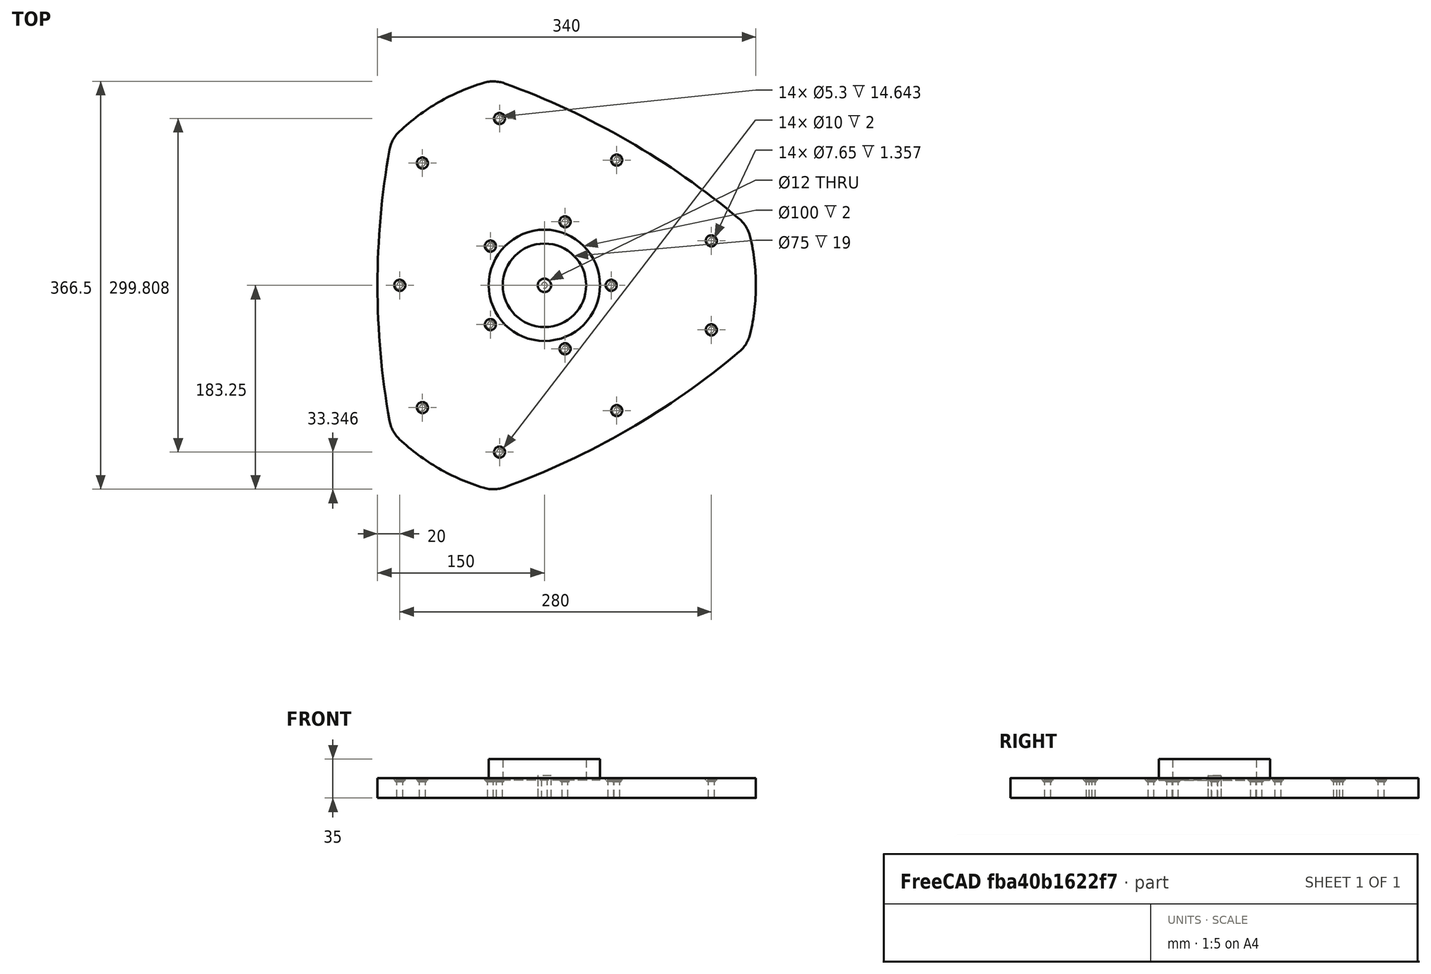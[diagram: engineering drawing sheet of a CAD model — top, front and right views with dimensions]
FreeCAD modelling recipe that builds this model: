
FCSTD DOCUMENT  (FreeCAD 1.1R38827 (Git))
Label: composit_stand3_basement_amplifier_model
License: All rights reserved
LicenseURL: http://en.wikipedia.org/wiki/All_rights_reserved
objects: Part::FeaturePython×6, App::Link×5, PartDesign::CoordinateSystem×3, PartDesign::SubShapeBinder×2, Part::Mirroring×1, Part::Compound×1, PartDesign::Pad×1, Part::Cylinder×1, Part::MultiFuse×1, PartDesign::Boolean×1, PartDesign::Body×1
note: 21 computed .brp shape members not serialized (recipe doc carries the construction recipe); baked Part::Feature solids carry a one-line shape summary decoded from their .brp
EXTERNAL_REF file=composit_stand3_basement_amplifier_main.FCStd obj=Sketch
EXTERNAL_REF file=composit_stand3_basement_amplifier_main.FCStd obj=Join001
EXTERNAL_REF file=composit_stand3_basement_amplifier_main.FCStd obj=Cylinder
EXTERNAL_REF file=composit_stand3_basement_bearing_holder_main.FCStd obj=Placment
EXTERNAL_REF file=../bearing_d100.FCStd obj=Body
EXTERNAL_REF file=composit_stand3_basement_amplifier_main.FCStd obj=Body

FEATURE [PartDesign::SubShapeBinder] Binder
  BindCopyOnChange = 0
  BindMode = 0
  ClaimChildren = false
  Fuse = false
  MakeFace = true
  OffsetFill = false
  OffsetIntersection = false
  OffsetJoinType = 0
  OffsetOpenResult = false
  PartialLoad = false
  Relative = true
  Support = -> [<external composit_stand3_basement_amplifier_main.FCStd>#Sketch]
  _Version = 2
FEATURE [Part::Mirroring] Part__Mirroring  label="Binder (Mirror #1)"
  Base = (0,0,0)
  Normal = (0,1,0)
  Source = -> Binder
FEATURE [Part::FeaturePython] PolarArray  # WARN: FeaturePython — macro-defined, semantics opaque (R4)
  Alignment = 0
  AttacherType = Attacher::AttachEngine3D
  CellStart = A1
  Count = 3
  DistributionLaw = 0
  EndInclusive = false
  ExposePlacement = false
  FlipX = false
  FlipZ = false
  GeneratorMode = 0
  MarkerShape = 1
  MarkerSize = 0
  NumElements = 3
  OrientMode = 2
  Radius = 100
  Reverse = false
  SpanEnd = 360
  SpanStart = 0
  Step = 120
  Type = lattice2PolarArray2.PolarArray
  UseArcRadius = false
  UseArcRange = 0
  VSGVersion = 1
  Values = 0.0 | 120.0 | 240.0
  ValuesSource = 2
  isLattice = 1
FEATURE [Part::Compound] Compound
  Links = -> [Binder,Part__Mirroring]
FEATURE [Part::FeaturePython] Populate  label="Populate PolarArray with Compound"  # WARN: FeaturePython — macro-defined, semantics opaque (R4)
  Copying = 0
  ExposePlacement = false
  MarkerShape = 1
  MarkerSize = 0
  NumElements = 0
  Object = -> Compound
  OutputCompounding = 1
  PlacementsTo = -> PolarArray
  Referencing = 1
  Type = lattice2PopulateCopies.LatticePopulateCopies
  isLattice = 0
FEATURE [Part::FeaturePython] Connect  # WARN: FeaturePython — macro-defined, semantics opaque (R4)
  Objects = -> [Populate]
  Tolerance = 0
FEATURE [PartDesign::SubShapeBinder] Binder001
  BindCopyOnChange = 0
  BindMode = 0
  ClaimChildren = true
  Context = -> Body [Binder001.]
  Fuse = false
  MakeFace = false
  OffsetFill = false
  OffsetIntersection = false
  OffsetJoinType = 0
  OffsetOpenResult = false
  PartialLoad = false
  Relative = true
  Support = -> [Connect]
  _Version = 2
FEATURE [PartDesign::Pad] Pad
  Direction = (0,0,1)
  Length = 18
  Length2 = 10
  Profile = -> Binder001
  Refine = true
  Suppressed = false
  Type = 0
FEATURE [App::Link] Link  label="Populate PolarArray with Join"
  LinkedObject = -> <external composit_stand3_basement_amplifier_main.FCStd>#Join001
FEATURE [Part::Cylinder] Cylinder  label="hole_5,2_mm"
  Angle = 360
  AttacherType = Attacher::AttachEngine3D
  FirstAngle = 0
  Height = 18
  Radius = 2.6
  SecondAngle = 0
FEATURE [Part::FeaturePython] Join  label="holes_placements"  # WARN: FeaturePython — macro-defined, semantics opaque (R4)
  ExposePlacement = false
  Interleave = false
  Links = -> [Link]
  MarkerShape = 1
  MarkerSize = 0
  NumElements = 14
  Type = lattice2JoinArrays.JoinArrays
  isLattice = 1
FEATURE [App::Link] Link001  label="axis_bolt"
  LinkedObject = -> <external composit_stand3_basement_amplifier_main.FCStd>#Cylinder
FEATURE [PartDesign::CoordinateSystem] Local_CS  label="bottom_LCS"
  AttacherType = Attacher::AttachEngine3D
  AttachmentSupport = -> [XY_Plane]
  MapMode = 5
FEATURE [PartDesign::CoordinateSystem] Local_CS001  label="top_LCS"
  AttacherType = Attacher::AttachEngine3D
  AttachmentOffset = pos=(0,0,18) rot=(0,0,1;0rad)
  AttachmentSupport = -> [XY_Plane]
  MapMode = 5
  Placement = pos=(0,0,18) rot=(0,0,1;0rad)
FEATURE [App::Link] Link002  label="bearing_placement"
  LinkTransform = true
  LinkedObject = -> <external composit_stand3_basement_bearing_holder_main.FCStd>#Placment
FEATURE [App::Link] Link003  label="Body"
  LinkedObject = -> <external ../bearing_d100.FCStd>#Body
FEATURE [Part::FeaturePython] Populate002  label="Populate bearing_placement with Body"  # WARN: FeaturePython — macro-defined, semantics opaque (R4)
  Copying = 0
  ExposePlacement = false
  MarkerShape = 1
  MarkerSize = 0
  NumElements = 0
  Object = -> Link003
  OutputCompounding = 2
  PlacementsTo = -> Link002
  Referencing = 0
  Type = lattice2PopulateCopies.LatticePopulateCopies
  isLattice = 0
FEATURE [PartDesign::CoordinateSystem] Local_CS002  label="bearing_LCS"
  AttacherType = Attacher::AttachEngine3D
  AttachmentOffset = pos=(0,0,16) rot=(0,0,1;0rad)
  AttachmentSupport = -> [XY_Plane]
  MapMode = 5
  Placement = pos=(0,0,16) rot=(0,0,1;0rad)
  expr: AttachmentOffset = <<bearing_placement>>.LinkedObject.Placement
FEATURE [App::Link] Link004  label="screw"
  LinkedObject = -> <external composit_stand3_basement_amplifier_main.FCStd>#Body
FEATURE [Part::FeaturePython] Populate001  label="Populate Populate PolarArray with Join with hole_5_mm"  # WARN: FeaturePython — macro-defined, semantics opaque (R4)
  Copying = 0
  ExposePlacement = false
  MarkerShape = 1
  MarkerSize = 0
  NumElements = 0
  Object = -> Link004
  OutputCompounding = 1
  PlacementsTo = -> Join
  Referencing = 0
  Type = lattice2PopulateCopies.LatticePopulateCopies
  isLattice = 0
FEATURE [Part::MultiFuse] Fusion
  Shapes = -> [Populate001,Link001,Populate002]
FEATURE [PartDesign::Boolean] Boolean
  BaseFeature = -> Pad
  Group = -> [Fusion]
  Suppressed = false
  Type = 1
  UsePlacement = true
FEATURE [PartDesign::Body] Body  label="amplifier"
  AllowCompound = false
  Group = -> [Binder001,Pad,Boolean,Local_CS,Local_CS001,Local_CS002]
  Origin = -> Origin
  Tip = -> Boolean

RESOLVED EXTERNAL PARTS (link-assembly join: the EXTERNAL_REF files above that resolve inside this repo's crawl, each included once):
---- part ../bearing_d100.FCStd = doc fcstd_fc5883dd0358 ----
FCSTD DOCUMENT  (FreeCAD 1.1R38827 (Git))
Label: bearing_d100
License: All rights reserved
LicenseURL: http://en.wikipedia.org/wiki/All_rights_reserved
objects: PartDesign::CoordinateSystem×2, Sketcher::SketchObject×1, PartDesign::SubShapeBinder×1, PartDesign::Revolution×1, PartDesign::Body×1
note: 9 computed .brp shape members not serialized (recipe doc carries the construction recipe); baked Part::Feature solids carry a one-line shape summary decoded from their .brp

FEATURE [Sketcher::SketchObject] Sketch  label="main_Sketch"
  ArcFitTolerance = 0
  FullyConstrained = true
  MakeInternals = false
  Placement = pos=(0,0,0) rot=(1,0,0;1.5708rad)
  sketch-geometry (4):
    g0: LineSegment StartX=37.5 StartY=0 StartZ=0 EndX=50 EndY=0 EndZ=0
    g1: LineSegment StartX=50 StartY=0 StartZ=0 EndX=50 EndY=19 EndZ=0
    g2: LineSegment StartX=50 StartY=19 StartZ=0 EndX=37.5 EndY=19 EndZ=0
    g3: LineSegment StartX=37.5 StartY=19 StartZ=0 EndX=37.5 EndY=0 EndZ=0
  constraints (12):
    c: Coincident(g0,g1)
    c: Coincident(g1,g2)
    c: Coincident(g2,g3)
    c: Coincident(g3,g0)
    c: Horizontal(g0)
    c: Horizontal(g2)
    c: Vertical(g1)
    c: Vertical(g3)
    c: PointOnObject(g0,g-1)
    c: DistanceX(g0) = 37.5  'min_r'
    c: DistanceX(g0) = 50  'max_r'
    c: DistanceY(g3,g3) = 19  'height'
FEATURE [PartDesign::SubShapeBinder] Binder
  BindCopyOnChange = 0
  BindMode = 0
  ClaimChildren = true
  Context = -> Body [Binder.]
  Fuse = false
  MakeFace = true
  OffsetFill = false
  OffsetIntersection = false
  OffsetJoinType = 0
  OffsetOpenResult = false
  PartialLoad = false
  Placement = pos=(0,0,0) rot=(1,0,0;1.5708rad)
  Relative = false
  Support = -> [Sketch]
  _Version = 2
  expr: Placement = Support[0][0].Placement
FEATURE [PartDesign::Revolution] Revolution
  Angle = 360
  Angle2 = 60
  Axis = (1e-16,1e-16,1)
  Base = (0,0,0)
  Placement = pos=(0,0,0) rot=(1,0,0;1.5708rad)
  Profile = -> Binder [Face1]
  ReferenceAxis = -> Z_Axis
  Reversed = true
  Suppressed = false
  Type = 0
FEATURE [PartDesign::CoordinateSystem] Local_CS  label="bottom_LCS"
  AttacherType = Attacher::AttachEngine3D
  AttachmentSupport = -> [XY_Plane]
  MapMode = 5
FEATURE [PartDesign::CoordinateSystem] Local_CS001  label="top_LCS"
  AttacherType = Attacher::AttachEngine3D
  AttachmentOffset = pos=(0,0,19) rot=(0,0,1;0rad)
  AttachmentSupport = -> [XY_Plane]
  MapMode = 5
  Placement = pos=(0,0,19) rot=(0,0,1;0rad)
  expr: .AttachmentOffset.Base.z = <<main_Sketch>>.Constraints.height
FEATURE [PartDesign::Body] Body  label="bearing_d100"
  AllowCompound = false
  Group = -> [Binder,Revolution,Local_CS,Local_CS001]
  Origin = -> Origin
  Tip = -> Revolution
---- part composit_stand3_basement_amplifier_main.FCStd = doc fcstd_07f535898d8e ----
FCSTD DOCUMENT  (FreeCAD 1.1R38827 (Git))
Label: composit_stand3_basement_amplifier_main
License: All rights reserved
LicenseURL: http://en.wikipedia.org/wiki/All_rights_reserved
objects: Part::FeaturePython×7, PartDesign::SubShapeBinder×2, Sketcher::SketchObject×2, App::Link×1, Part::Cylinder×1, PartDesign::Revolution×1, PartDesign::Body×1
note: 18 computed .brp shape members not serialized (recipe doc carries the construction recipe); baked Part::Feature solids carry a one-line shape summary decoded from their .brp
EXTERNAL_REF file=composit_stand3_basement_bottom_main.FCStd obj=Sketch
EXTERNAL_REF file=composit_stand3_basement_top_main.FCStd obj=Sketch
EXTERNAL_REF file=composit_stand3_basement_bearing_holder_main.FCStd obj=Join

FEATURE [PartDesign::SubShapeBinder] Binder
  BindCopyOnChange = 0
  BindMode = 0
  ClaimChildren = false
  Fuse = false
  MakeFace = true
  OffsetFill = false
  OffsetIntersection = false
  OffsetJoinType = 0
  OffsetOpenResult = false
  PartialLoad = false
  Relative = true
  Support = -> [<external composit_stand3_basement_bottom_main.FCStd>#Sketch]
  _Version = 2
FEATURE [PartDesign::SubShapeBinder] Binder001
  BindCopyOnChange = 0
  BindMode = 0
  ClaimChildren = false
  Fuse = false
  MakeFace = true
  OffsetFill = false
  OffsetIntersection = false
  OffsetJoinType = 0
  OffsetOpenResult = false
  PartialLoad = false
  Relative = true
  Support = -> [<external composit_stand3_basement_top_main.FCStd>#Sketch]
  _Version = 2
FEATURE [Sketcher::SketchObject] Sketch
  ArcFitTolerance = 0
  ExternalGeometry = -> [Binder001]
  FullyConstrained = true
  MakeInternals = false
  expr: Constraints[6] = <<composit_stand3_basement_bottom_main>>#<<basement_bottom_main_sketch>>.Constraints.min_r - 20 mm
  sketch-geometry (5):
    g0: LineSegment [constr] StartX=0 StartY=0 StartZ=0 EndX=75 EndY=129.904 EndZ=0
    g1: ArcOfCircle CenterX=-272.703 CenterY=-472.335 CenterZ=0 NormalX=0 NormalY=0 NormalZ=1 AngleXU=0 Radius=695.406 StartAngle=0.871298 EndAngle=1.0472
    g2: ArcOfCircle CenterX=155.708 CenterY=36.8099 CenterZ=0 NormalX=0 NormalY=0 NormalZ=1 AngleXU=0 Radius=30 StartAngle=0.232142 EndAngle=0.871298
    g3: ArcOfCircle CenterX=0 CenterY=0 CenterZ=0 NormalX=0 NormalY=0 NormalZ=1 AngleXU=0 Radius=190 StartAngle=0 EndAngle=0.232142
    g4: Circle [constr] CenterX=0 CenterY=0 CenterZ=0 NormalX=0 NormalY=0 NormalZ=1 AngleXU=0 Radius=545.406
  constraints (14):
    c: Coincident(g0,g-1)
    c: Angle(g0) = 1.0472
    c: Coincident(g1,g0)
    c: PointOnObject(g3,g-1)
    c: Tangent(g3,g2) = -1.5708
    c: Tangent(g2,g1) = -1.5708
    c: Distance(g0) = 150
    c: Coincident(g4,g0)
    c: PointOnObject(g-3,g4)
    c: Coincident(g1,g-3)
    c: DistanceX(g3) = 190
    c: Radius(g2) = 30
    c: PointOnObject(g3,g-1)
    c: PointOnObject(g3,g-2)
FEATURE [Part::FeaturePython] Placment  # WARN: FeaturePython — macro-defined, semantics opaque (R4)
  AttacherType = Attacher::AttachEngine3D
  ExposePlacement = true
  MarkerShape = 1
  MarkerSize = 20
  NumElements = 1
  Placement = pos=(65,112.583,0) rot=(0,0,1;0rad)
  Type = lattice2AttachablePlacement.AttachablePlacement
  isLattice = 1
  expr: .Placement.Base.y = .Placement.Base.x * tan(60)
FEATURE [Part::FeaturePython] Placment001  # WARN: FeaturePython — macro-defined, semantics opaque (R4)
  AttacherType = Attacher::AttachEngine3D
  ExposePlacement = true
  MarkerShape = 1
  MarkerSize = 20
  NumElements = 1
  Placement = pos=(150,40,0) rot=(0,0,1;0rad)
  Type = lattice2AttachablePlacement.AttachablePlacement
  isLattice = 1
FEATURE [Part::FeaturePython] Mirror  label="Mirror of Placment001"  # WARN: FeaturePython — macro-defined, semantics opaque (R4)
  ExposePlacement = false
  FlipX = false
  FlipY = true
  FlipZ = false
  MarkerShape = 1
  MarkerSize = 20
  NumElements = 1
  Object = -> Placment001
  ObjectTraversal = 0
  PivotPlacement = pos=(0,0,0) rot=(0,0,1;1.0472rad)
  Type = lattice2Mirror.LatticeMirror
  isLattice = 1
FEATURE [Part::FeaturePython] Join  # WARN: FeaturePython — macro-defined, semantics opaque (R4)
  ExposePlacement = false
  Interleave = false
  Links = -> [Placment,Placment001,Mirror]
  MarkerShape = 1
  MarkerSize = 0
  NumElements = 3
  Type = lattice2JoinArrays.JoinArrays
  isLattice = 1
FEATURE [Part::FeaturePython] PolarArray  # WARN: FeaturePython — macro-defined, semantics opaque (R4)
  Alignment = 0
  AttacherType = Attacher::AttachEngine3D
  CellStart = A1
  Count = 3
  DistributionLaw = 0
  EndInclusive = false
  ExposePlacement = false
  FlipX = false
  FlipZ = false
  GeneratorMode = 0
  MarkerShape = 1
  MarkerSize = 0
  NumElements = 3
  OrientMode = 2
  Radius = 100
  Reverse = false
  SpanEnd = 360
  SpanStart = 0
  Step = 120
  Type = lattice2PolarArray2.PolarArray
  UseArcRadius = false
  UseArcRange = 0
  VSGVersion = 1
  Values = 0.0 | 120.0 | 240.0
  ValuesSource = 2
  isLattice = 1
FEATURE [Part::FeaturePython] Populate  label="Populate PolarArray with Join"  # WARN: FeaturePython — macro-defined, semantics opaque (R4)
  Copying = 0
  ExposePlacement = false
  MarkerShape = 1
  MarkerSize = 0
  NumElements = 9
  Object = -> Join
  OutputCompounding = 0
  PlacementsTo = -> PolarArray
  Referencing = 1
  Type = lattice2PopulateCopies.LatticePopulateCopies
  isLattice = 1
FEATURE [App::Link] Link  label="bearing_holes_placements"
  LinkedObject = -> <external composit_stand3_basement_bearing_holder_main.FCStd>#Join
FEATURE [Part::FeaturePython] Join001  label="holes_placements"  # WARN: FeaturePython — macro-defined, semantics opaque (R4)
  ExposePlacement = false
  Interleave = false
  Links = -> [Populate,Link]
  MarkerShape = 1
  MarkerSize = 0
  NumElements = 14
  Type = lattice2JoinArrays.JoinArrays
  isLattice = 1
FEATURE [Part::Cylinder] Cylinder  label="axis_bolt"
  Angle = 360
  AttacherType = Attacher::AttachEngine3D
  FirstAngle = 0
  Height = 20
  Radius = 6
  SecondAngle = 0
FEATURE [Sketcher::SketchObject] Sketch001
  ArcFitTolerance = 0
  AttachmentSupport = -> [XZ_Plane]
  FullyConstrained = true
  MakeInternals = false
  MapMode = 5
  Placement = pos=(0,0,0) rot=(1,0,0;1.5708rad)
  sketch-geometry (9):
    g0: LineSegment StartX=0 StartY=0 StartZ=0 EndX=2.65 EndY=0 EndZ=0
    g1: LineSegment StartX=2.65 StartY=0 StartZ=0 EndX=2.65 EndY=14.6432 EndZ=0
    g2: LineSegment StartX=2.65 StartY=14.6432 StartZ=0 EndX=3.825 EndY=14.6432 EndZ=0
    g3: LineSegment StartX=3.825 StartY=14.6432 StartZ=0 EndX=3.825 EndY=16 EndZ=0
    g4: LineSegment StartX=3.825 StartY=16 StartZ=0 EndX=5 EndY=16 EndZ=0
    g5: LineSegment StartX=5 StartY=16 StartZ=0 EndX=5 EndY=18 EndZ=0
    g6: LineSegment StartX=5 StartY=18 StartZ=0 EndX=0 EndY=18 EndZ=0
    g7: LineSegment StartX=0 StartY=18 StartZ=0 EndX=0 EndY=0 EndZ=0
    g8: LineSegment [constr] StartX=2.65 StartY=14.6432 StartZ=0 EndX=5 EndY=16 EndZ=0
  constraints (25):
    c: Coincident(g-1,g0)
    c: PointOnObject(g0,g-1)
    c: Coincident(g0,g1)
    c: Vertical(g1)
    c: Coincident(g1,g2)
    c: Horizontal(g2)
    c: Coincident(g2,g3)
    c: Vertical(g3)
    c: Coincident(g3,g4)
    c: Horizontal(g4)
    c: Coincident(g4,g5)
    c: Vertical(g5)
    c: Coincident(g5,g6)
    c: Horizontal(g6)
    c: Coincident(g6,g7)
    c: Coincident(g7,g0)
    c: Vertical(g7)
    c: DistanceX(g0) = 2.65
    c: Coincident(g8,g1)
    c: Coincident(g8,g4)
    c: Angle(g8) = 0.523599
    c: Equal(g4,g2)
    c: DistanceY(g5,g5) = 2
    c: DistanceX(g5) = 5
    c: DistanceY(g6) = 18
FEATURE [PartDesign::Revolution] Revolution
  Angle = 360
  Angle2 = 60
  Axis = (0,2e-16,1)
  Base = (0,0,0)
  Placement = pos=(0,0,0) rot=(1,0,0;1.5708rad)
  Profile = -> Sketch001
  ReferenceAxis = -> Sketch001 [V_Axis]
  Reversed = true
  Suppressed = false
  Type = 0
FEATURE [PartDesign::Body] Body  label="screw"
  AllowCompound = false
  Group = -> [Sketch001,Revolution]
  Origin = -> Origin
  Tip = -> Revolution
---- part composit_stand3_basement_bearing_holder_main.FCStd = doc fcstd_dd1238283213 ----
FCSTD DOCUMENT  (FreeCAD 1.1R38827 (Git))
Label: composit_stand3_basement_bearing_holder_main
License: All rights reserved
LicenseURL: http://en.wikipedia.org/wiki/All_rights_reserved
objects: Part::FeaturePython×3, Sketcher::SketchObject×1
note: 5 computed .brp shape members not serialized (recipe doc carries the construction recipe); baked Part::Feature solids carry a one-line shape summary decoded from their .brp
EXTERNAL_REF file=../bearing_d100.FCStd obj=Sketch

FEATURE [Sketcher::SketchObject] Sketch
  ArcFitTolerance = 0
  FullyConstrained = true
  MakeInternals = false
  expr: .Constraints.d = <<bearing_d100>>#<<main_Sketch>>.Constraints.max_r * 2 + 40 mm
  sketch-geometry (1):
    g0: Circle CenterX=0 CenterY=0 CenterZ=0 NormalX=0 NormalY=0 NormalZ=1 AngleXU=0 Radius=70
  constraints (2):
    c: Coincident(g0,g-1)
    c: Diameter(g0) = 140  'd'
FEATURE [Part::FeaturePython] PolarArray  # WARN: FeaturePython — macro-defined, semantics opaque (R4)
  Alignment = 0
  AttacherType = Attacher::AttachEngine3D
  CellStart = A1
  Count = 5
  DistributionLaw = 0
  EndInclusive = false
  ExposePlacement = false
  FlipX = false
  FlipZ = false
  GeneratorMode = 0
  MarkerShape = 1
  MarkerSize = 0
  NumElements = 5
  OrientMode = 2
  Radius = 60
  Reverse = false
  SpanEnd = 360
  SpanStart = 0
  Step = 72
  Type = lattice2PolarArray2.PolarArray
  UseArcRadius = false
  UseArcRange = 0
  VSGVersion = 1
  Values = 0.0 | 72.0 | 144.0 | 216.0 | 288.0
  ValuesSource = 2
  isLattice = 1
  expr: Radius = <<bearing_d100>>#<<main_Sketch>>.Constraints.max_r + 10 mm
FEATURE [Part::FeaturePython] Join  label="holes_placements"  # WARN: FeaturePython — macro-defined, semantics opaque (R4)
  ExposePlacement = false
  Interleave = false
  Links = -> [PolarArray]
  MarkerShape = 1
  MarkerSize = 0
  NumElements = 5
  Type = lattice2JoinArrays.JoinArrays
  isLattice = 1
FEATURE [Part::FeaturePython] Placment  label="bearing_placement"  # WARN: FeaturePython — macro-defined, semantics opaque (R4)
  AttacherType = Attacher::AttachEngine3D
  ExposePlacement = true
  MarkerShape = 1
  MarkerSize = 10
  NumElements = 1
  Placement = pos=(0,0,16) rot=(0,0,1;0rad)
  Type = lattice2AttachablePlacement.AttachablePlacement
  isLattice = 1
